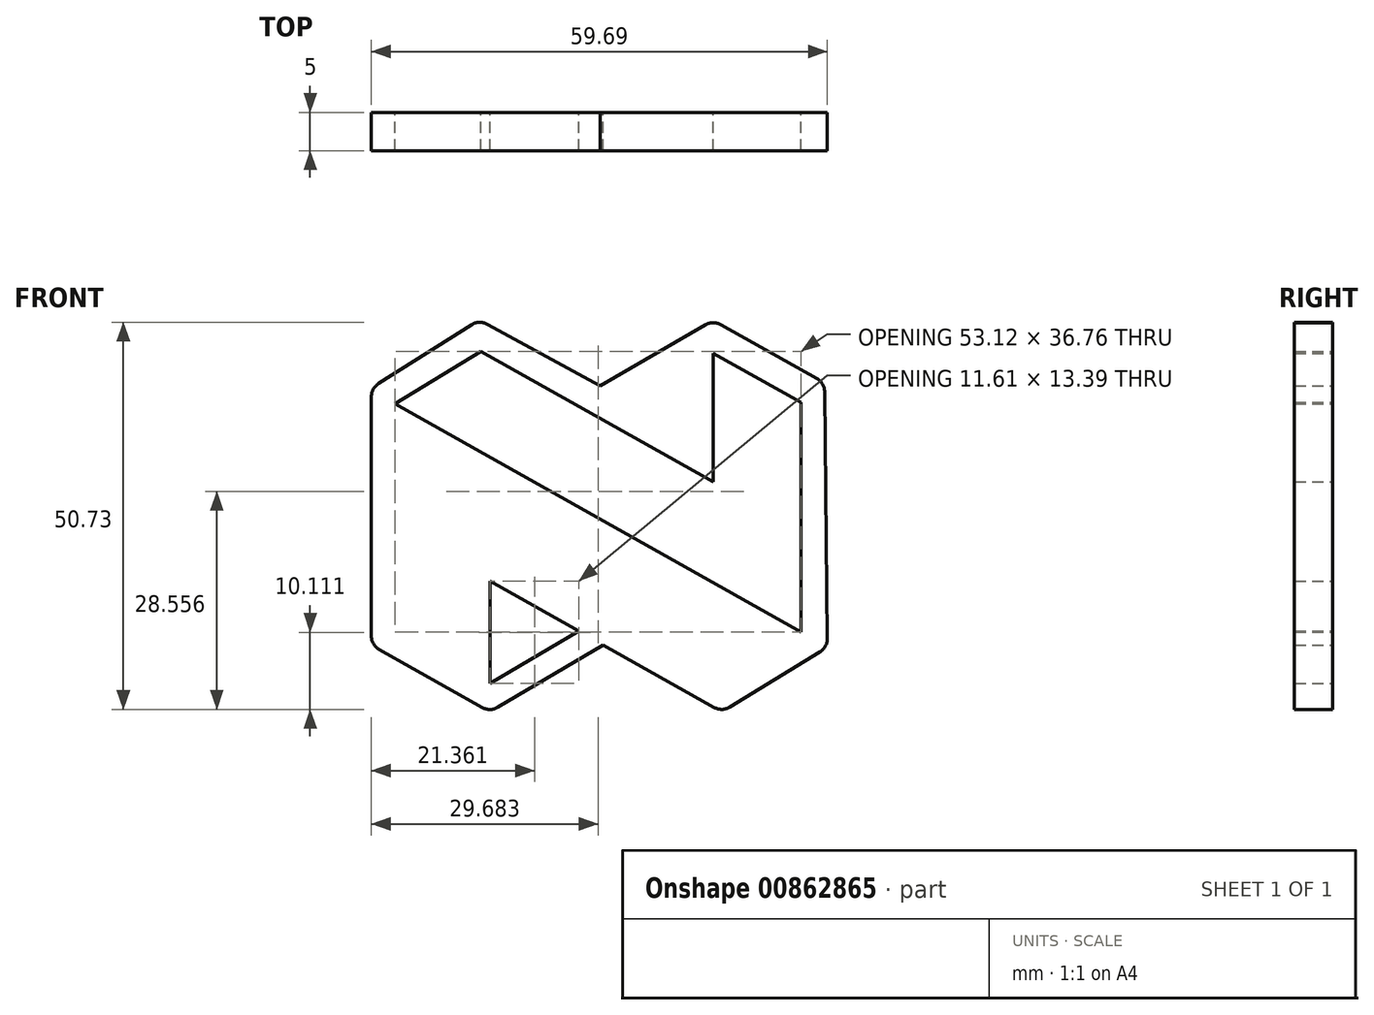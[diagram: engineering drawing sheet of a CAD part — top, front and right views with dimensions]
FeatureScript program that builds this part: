
annotation { "Feature Type Name" : "Feature", "Feature Type Description" : "" }
export const myFeature = defineFeature(function(context is Context, id is Id, definition is map)
    precondition{}
    {
        {
            var Q0;
            Q0=qCreatedBy(makeId("Front.planeOp"),FACE);
            var sketch = newSketch(context, id + "F0", { "sketchPlane" : qUnion([Q0])});
            skPoint(sketch, "E0.middle", {"position": v(0, 0) * mm});
            skLineSegment(sketch, "E1", {"start": v(0.43, 17.02) * mm, "end": v(15.22, 25.59) * mm});
            skLineSegment(sketch, "E2", {"start": v(15.22, 25.59) * mm, "end": v(29.8, 17.39) * mm});
            skLineSegment(sketch, "E3", {"start": v(0.84, -16.96) * mm, "end": v(16.4, -25.71) * mm});
            skLineSegment(sketch, "E4", {"start": v(16.4, -25.71) * mm, "end": v(30.19, -17.26) * mm});
            skLineSegment(sketch, "E5", {"start": v(30.19, -17.26) * mm, "end": v(29.8, 17.39) * mm});
            skLineSegment(sketch, "E6", {"start": v(0.84, -16.96) * mm, "end": v(-13.96, -25.71) * mm});
            skLineSegment(sketch, "E7", {"start": v(-13.96, -25.71) * mm, "end": v(-29.52, -16.96) * mm});
            skLineSegment(sketch, "E8", {"start": v(-29.52, -16.96) * mm, "end": v(-29.52, 16.7) * mm});
            skLineSegment(sketch, "E9", {"start": v(-29.52, 16.7) * mm, "end": v(-15.42, 25.64) * mm});
            skLineSegment(sketch, "E10", {"start": v(-15.42, 25.64) * mm, "end": v(0.43, 17.02) * mm});
            skLineSegment(sketch, "E11", {"start": v(15.22, 21.29) * mm, "end": v(26.72, 14.82) * mm});
            skLineSegment(sketch, "E12", {"start": v(26.72, 14.82) * mm, "end": v(26.72, -15.22) * mm});
            skLineSegment(sketch, "E13", {"start": v(26.72, -15.22) * mm, "end": v(-26.4, 14.66) * mm});
            skLineSegment(sketch, "E14", {"start": v(-26.4, 14.66) * mm, "end": v(-15.18, 21.54) * mm});
            skLineSegment(sketch, "E15", {"start": v(-15.18, 21.54) * mm, "end": v(15.22, 4.43) * mm});
            skLineSegment(sketch, "E16", {"start": v(15.22, 4.43) * mm, "end": v(15.22, 21.29) * mm});
            skLineSegment(sketch, "E17", {"start": v(-13.96, -21.98) * mm, "end": v(-2.35, -15.12) * mm});
            skLineSegment(sketch, "E18", {"start": v(-2.35, -15.12) * mm, "end": v(-13.96, -8.6) * mm});
            skLineSegment(sketch, "E19", {"start": v(-13.96, -8.6) * mm, "end": v(-13.96, -21.98) * mm});
            skSolve(sketch);
        }
        {
            var Q0;
            Q0=makeQuery(id+"F0.imprint","IMPRINT",FACE,{"disambiguationData":[TD([[makeQuery(id+"F0.imprint","IMPRINT",EDGE,{"derivedFrom":sQuery(id+"F0.wireOp",EDGE,"E1")}),-1.0]])]});
            extrude(context, id + "F1", {"entities" : qUnion([Q0]), "depth" : 5 * mm, "offsetDistance" : 25 * mm});
        }
        {
            var Q0;
            Q0=makeQuery(id+"F1.opExtrude","SWEPT_EDGE",EDGE,{"disambiguationData":[OSD([sQuery(id+"F0.wireOp",EDGE,"E1"),sQuery(id+"F0.wireOp",EDGE,"E2")])]});
            var Q1;
            Q1=makeQuery(id+"F1.opExtrude","SWEPT_EDGE",EDGE,{"disambiguationData":[OSD([sQuery(id+"F0.wireOp",EDGE,"E2"),sQuery(id+"F0.wireOp",EDGE,"E5")])]});
            var Q2;
            Q2=makeQuery(id+"F1.opExtrude","SWEPT_EDGE",EDGE,{"disambiguationData":[OSD([sQuery(id+"F0.wireOp",EDGE,"E4"),sQuery(id+"F0.wireOp",EDGE,"E5")])]});
            var Q3;
            Q3=makeQuery(id+"F1.opExtrude","SWEPT_EDGE",EDGE,{"disambiguationData":[OSD([sQuery(id+"F0.wireOp",EDGE,"E9"),sQuery(id+"F0.wireOp",EDGE,"E10")])]});
            var Q4;
            Q4=makeQuery(id+"F1.opExtrude","SWEPT_EDGE",EDGE,{"disambiguationData":[OSD([sQuery(id+"F0.wireOp",EDGE,"E3"),sQuery(id+"F0.wireOp",EDGE,"E4")])]});
            var Q5;
            Q5=makeQuery(id+"F1.opExtrude","SWEPT_EDGE",EDGE,{"disambiguationData":[OSD([sQuery(id+"F0.wireOp",EDGE,"E6"),sQuery(id+"F0.wireOp",EDGE,"E7")])]});
            var Q6;
            Q6=makeQuery(id+"F1.opExtrude","SWEPT_EDGE",EDGE,{"disambiguationData":[OSD([sQuery(id+"F0.wireOp",EDGE,"E7"),sQuery(id+"F0.wireOp",EDGE,"E8")])]});
            var Q7;
            Q7=makeQuery(id+"F1.opExtrude","SWEPT_EDGE",EDGE,{"disambiguationData":[OSD([sQuery(id+"F0.wireOp",EDGE,"E8"),sQuery(id+"F0.wireOp",EDGE,"E9")])]});
            fillet(context, id + "F2", {"entities" : qUnion([Q0, Q1, Q2, Q3, Q4, Q5, Q6, Q7]), "radius" : 2 * mm, "tangentPropagation" : true, "allowEdgeOverflow" : false});
        }
    });
